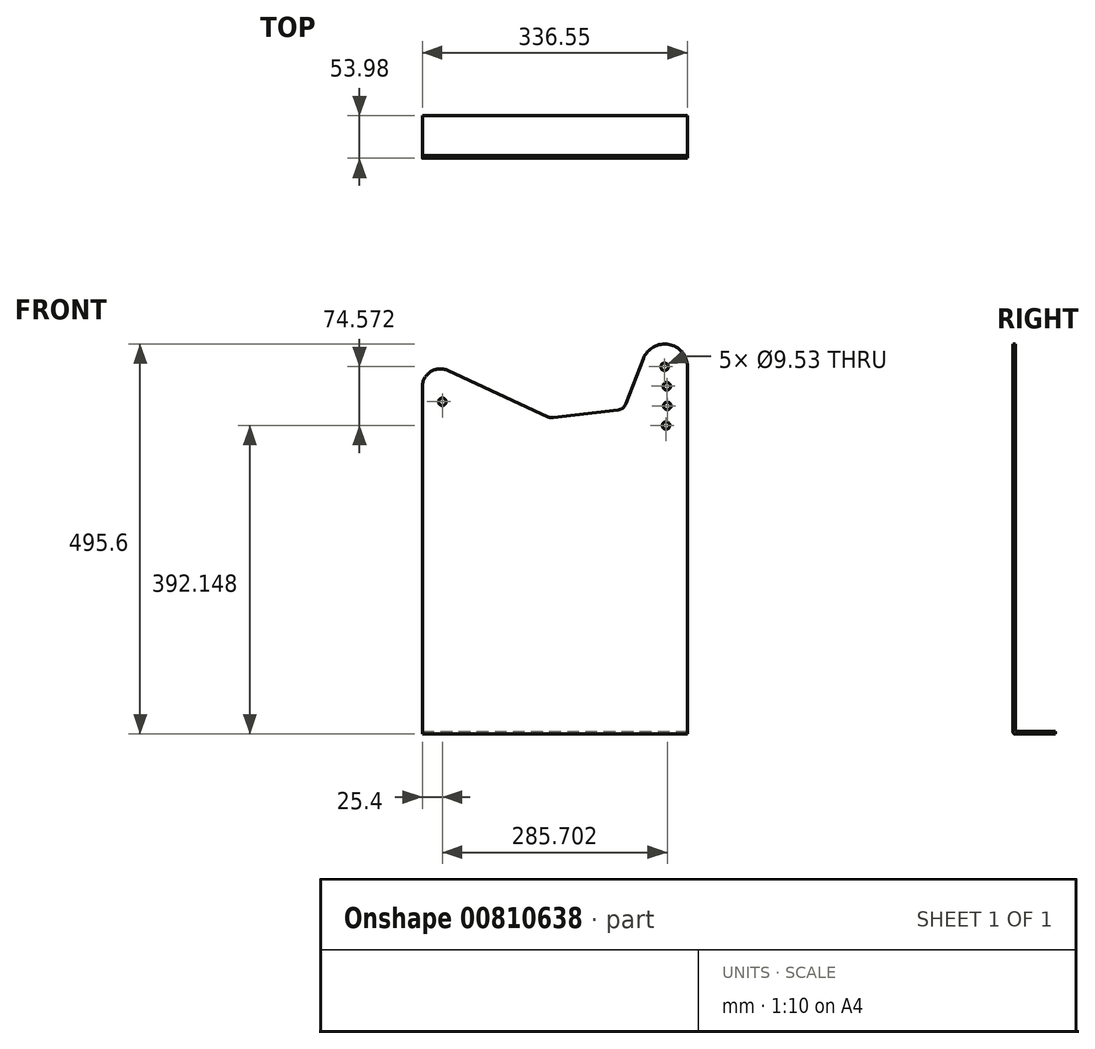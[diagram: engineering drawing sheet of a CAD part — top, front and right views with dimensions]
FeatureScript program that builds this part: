
annotation { "Feature Type Name" : "Feature", "Feature Type Description" : "" }
export const myFeature = defineFeature(function(context is Context, id is Id, definition is map)
    precondition{}
    {
        {
            var Q0;
            Q0=qCreatedBy(makeId("Front.planeOp"),FACE);
            var sketch = newSketch(context, id + "F0", { "sketchPlane" : qUnion([Q0])});
            skLineSegment(sketch, "E0", {"start": v(0, 0) * mm, "end": v(790, 0) * mm});
            skSolve(sketch);
        }
        {
            var Q0;
            Q0=qCreatedBy(makeId("Front.planeOp"),FACE);
            var sketch = newSketch(context, id + "F1", { "sketchPlane" : qUnion([Q0])});
            skLineSegment(sketch, "E1.bottom", {"start": v(0, 0) * mm, "end": v(336.55, 0) * mm});
            skLineSegment(sketch, "E1.top", {"start": v(0, 508) * mm, "end": v(336.55, 508) * mm, "construction": true});
            skLineSegment(sketch, "E1.left", {"start": v(0, 0) * mm, "end": v(0, 508) * mm});
            skLineSegment(sketch, "E1.right", {"start": v(336.55, 0) * mm, "end": v(336.55, 508) * mm});
            skCircle(sketch, "E2", {"center": v(25.4, 419.1) * mm, "radius": 4.76 * mm});
            skCircle(sketch, "E3", {"center": v(307.67, 463.55) * mm, "radius": 4.76 * mm});
            skCircle(sketch, "E4", {"center": v(25.4, 419.1) * mm, "radius": 285.75 * mm, "construction": true});
            skCircle(sketch, "E5", {"center": v(310.47, 438.78) * mm, "radius": 4.76 * mm});
            skCircle(sketch, "E6", {"center": v(311.1, 413.86) * mm, "radius": 4.76 * mm});
            skCircle(sketch, "E7", {"center": v(309.56, 388.98) * mm, "radius": 4.76 * mm});
            skLineSegment(sketch, "E8", {"start": v(25.4, 419.1) * mm, "end": v(307.67, 463.55) * mm, "construction": true});
            skLineSegment(sketch, "E9", {"start": v(25.4, 419.1) * mm, "end": v(310.47, 438.78) * mm, "construction": true});
            skLineSegment(sketch, "E10", {"start": v(25.4, 419.1) * mm, "end": v(311.1, 413.86) * mm, "construction": true});
            skLineSegment(sketch, "E11", {"start": v(25.4, 419.1) * mm, "end": v(309.56, 388.98) * mm, "construction": true});
            skLineSegment(sketch, "E12", {"start": v(255.8, 409.53) * mm, "end": v(166.35, 398.86) * mm});
            skLineSegment(sketch, "E13", {"start": v(159.51, 399.95) * mm, "end": v(32.46, 458.77) * mm});
            skPoint(sketch, "E14.visualSharp", {"position": v(0, 473.8) * mm});
            skArc(sketch, "E14.filletArc", {"start": v(32.46, 458.77) * mm, "mid": v(10.55, 457.29) * mm, "end": v(0, 438.03) * mm});
            skPoint(sketch, "E15.visualSharp", {"position": v(349.88, 465.88) * mm});
            skPoint(sketch, "E16.visualSharp", {"position": v(162.78, 398.44) * mm});
            skPoint(sketch, "E17.visualSharp", {"position": v(255.8, 409.53) * mm});
            skArc(sketch, "E18", {"start": v(336.55, 463.55) * mm, "mid": v(312.97, 491.94) * mm, "end": v(280.74, 473.97) * mm});
            skLineSegment(sketch, "E19", {"start": v(255.8, 409.53) * mm, "end": v(280.74, 473.97) * mm});
            skLineSegment(sketch, "E20", {"start": v(159.51, 399.95) * mm, "end": v(162.78, 398.44) * mm});
            skLineSegment(sketch, "E21", {"start": v(166.35, 398.86) * mm, "end": v(162.78, 398.44) * mm});
            skSolve(sketch);
        }
        {
            var Q0;
            {var subQ0=sQuery(id+"F1.wireOp",EDGE,"E1.bottom");Q0=makeQuery(id+"F1.imprint","IMPRINT",FACE,{"disambiguationData":[TD([[makeQuery(id+"F1.imprint","IMPRINT",EDGE,{"derivedFrom":subQ0}),1.0]])]});}
            extrude(context, id + "F2", {"entities" : qUnion([Q0]), "depth" : 3.17 * mm, "offsetDistance" : 25.4 * mm});
        }
        {
            var Q0;
            Q0=makeQuery(id+"F2.opExtrude","SWEPT_EDGE",EDGE,{"disambiguationData":[OSD([sQuery(id+"F1.wireOp",EDGE,"E20"),sQuery(id+"F1.wireOp",EDGE,"E21")])]});
            var Q1;
            Q1=makeQuery(id+"F2.opExtrude","SWEPT_EDGE",EDGE,{"disambiguationData":[OSD([sQuery(id+"F1.wireOp",EDGE,"E12"),sQuery(id+"F1.wireOp",EDGE,"E19")])]});
            fillet(context, id + "F3", {"entities" : qUnion([Q0, Q1]), "radius" : 12.7 * mm, "tangentPropagation" : true, "allowEdgeOverflow" : false});
        }
        {
            var Q0;
            Q0=qCreatedBy(makeId("Right.planeOp"),FACE);
            var sketch = newSketch(context, id + "F4", { "sketchPlane" : qUnion([Q0])});
            skLineSegment(sketch, "E22.0", {"start": v(-3.18, 0) * mm, "end": v(0, 0) * mm});
            skLineSegment(sketch, "E23.bottom", {"start": v(-3.18, 0) * mm, "end": v(50.8, 0) * mm});
            skLineSegment(sketch, "E23.top", {"start": v(-3.18, -3.18) * mm, "end": v(50.8, -3.18) * mm});
            skLineSegment(sketch, "E23.left", {"start": v(-3.18, 0) * mm, "end": v(-3.18, -3.18) * mm});
            skLineSegment(sketch, "E23.right", {"start": v(50.8, 0) * mm, "end": v(50.8, -3.18) * mm});
            skSolve(sketch);
        }
        {
            var Q0;
            Q0=makeQuery(id+"F4.imprint","IMPRINT",FACE,{"disambiguationData":[TD([[makeQuery(id+"F4.imprint","IMPRINT",EDGE,{"derivedFrom":sQuery(id+"F4.wireOp",EDGE,"E23.top")}),1.0]])]});
            var Q1;
            Q1=makeQuery(id+"F2.opExtrude","SWEPT_FACE",FACE,{"disambiguationData":[OSD([sQuery(id+"F1.wireOp",EDGE,"E1.right")])]});
            extrude(context, id + "F5", {"entities" : qUnion([Q0]), "operationType" : NewBodyOperationType.ADD, "endBound" : BoundingType.UP_TO_SURFACE, "depth" : 25.4 * mm, "endBoundEntityFace" : qUnion([Q1]), "offsetDistance" : 25.4 * mm});
        }
        {
            var Q0;
            Q0=makeQuery(id+"F5.opExtrude","SWEPT_EDGE",EDGE,{"disambiguationData":[OSD([sQuery(id+"F4.wireOp",EDGE,"E23.top"),sQuery(id+"F4.wireOp",EDGE,"E23.left")])]});
            fillet(context, id + "F6", {"entities" : qUnion([Q0]), "radius" : 3.17 * mm, "tangentPropagation" : true, "allowEdgeOverflow" : false});
        }
    });
